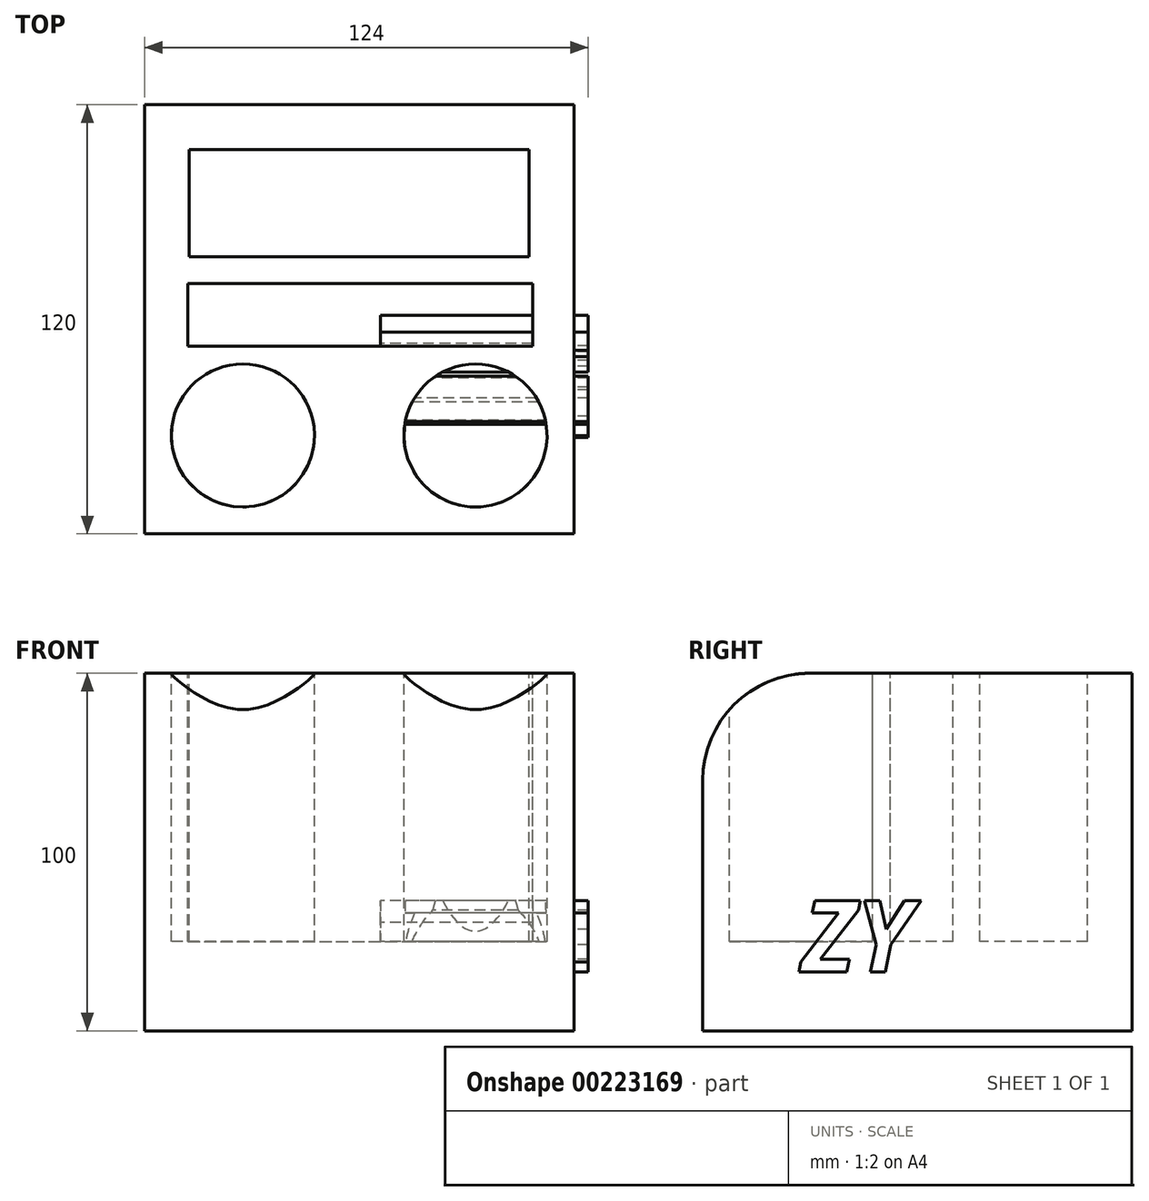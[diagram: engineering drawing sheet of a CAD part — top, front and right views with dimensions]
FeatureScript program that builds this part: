
annotation { "Feature Type Name" : "Feature", "Feature Type Description" : "" }
export const myFeature = defineFeature(function(context is Context, id is Id, definition is map)
    precondition{}
    {
        {
            var Q0;
            Q0=qCreatedBy(makeId("Top.planeOp"),FACE);
            var sketch = newSketch(context, id + "F0", { "sketchPlane" : qUnion([Q0])});
            skLineSegment(sketch, "E0.bottom", {"start": v(54, -65.16) * mm, "end": v(-66, -65.16) * mm});
            skLineSegment(sketch, "E0.top", {"start": v(54, 54.84) * mm, "end": v(-66, 54.84) * mm});
            skLineSegment(sketch, "E0.left", {"start": v(54, -65.16) * mm, "end": v(54, 54.84) * mm});
            skLineSegment(sketch, "E0.right", {"start": v(-66, -65.16) * mm, "end": v(-66, 54.84) * mm});
            skSolve(sketch);
        }
        {
            var Q0;
            Q0=qCreatedBy(makeId("Top.planeOp"),FACE);
            var sketch = newSketch(context, id + "F1", { "sketchPlane" : qUnion([Q0])});
            skLineSegment(sketch, "E1.bottom", {"start": v(-53.5, 42.34) * mm, "end": v(41.5, 42.34) * mm});
            skLineSegment(sketch, "E1.top", {"start": v(-53.5, 12.34) * mm, "end": v(41.5, 12.34) * mm});
            skLineSegment(sketch, "E1.left", {"start": v(-53.5, 42.34) * mm, "end": v(-53.5, 12.34) * mm});
            skLineSegment(sketch, "E1.right", {"start": v(41.5, 42.34) * mm, "end": v(41.5, 12.34) * mm});
            skCircle(sketch, "E2", {"center": v(-38.5, -37.66) * mm, "radius": 20 * mm});
            skCircle(sketch, "E3", {"center": v(26.5, -37.66) * mm, "radius": 20 * mm});
            skLineSegment(sketch, "E4.bottom", {"start": v(-53.93, 4.84) * mm, "end": v(42.46, 4.84) * mm});
            skLineSegment(sketch, "E4.top", {"start": v(-53.93, -12.66) * mm, "end": v(42.46, -12.66) * mm});
            skLineSegment(sketch, "E4.left", {"start": v(-53.93, 4.84) * mm, "end": v(-53.93, -12.66) * mm});
            skLineSegment(sketch, "E4.right", {"start": v(42.46, 4.84) * mm, "end": v(42.46, -12.66) * mm});
            skSolve(sketch);
        }
        {
            var Q0;
            Q0 = qSketchRegion(id + "F0", true);
            extrude(context, id + "F2", {"entities" : qUnion([Q0]), "oppositeDirection" : true, "depth" : 100 * mm});
        }
        {
            var Q0;
            Q0 = qSketchRegion(id + "F1", true);
            extrude(context, id + "F3", {"entities" : qUnion([Q0]), "operationType" : NewBodyOperationType.REMOVE, "oppositeDirection" : true, "depth" : 75 * mm});
        }
        {
            var Q0;
            Q0=makeQuery(id+"F2.opExtrude","CAP_EDGE",EDGE,{"disambiguationData":[OSD([sQuery(id+"F0.wireOp",EDGE,"E0.bottom")])],"isStart":true});
            fillet(context, id + "F4", {"entities" : qUnion([Q0]), "radius" : 30 * mm, "tangentPropagation" : true, "allowEdgeOverflow" : false});
        }
        {
            var Q0;
            Q0=qCreatedBy(makeId("Right.planeOp"),FACE);
            var sketch = newSketch(context, id + "F5", { "sketchPlane" : qUnion([Q0])});
            skText(sketch, "E5", { "text": "ZY", "fontName": "OpenSans-BoldItalic.ttf"});
            const initialGuessF5  = {"E5": [-0.03744, -0.08354, 1, 0, 0.02014]};
            skSetInitialGuess(sketch, initialGuessF5);
            skSolve(sketch);
        }
        {
            var Q0;
            Q0 = qSketchRegion(id + "F5", true);
            extrude(context, id + "F6", {"entities" : qUnion([Q0]), "operationType" : NewBodyOperationType.ADD, "depth" : 58 * mm});
        }
    });
